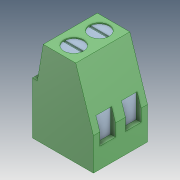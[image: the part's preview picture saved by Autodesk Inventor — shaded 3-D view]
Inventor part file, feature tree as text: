
AUTODESK INVENTOR PART (.ipt)
format: ipt  version: 2020 (Build 240168000, 168)  size: 202,752 bytes
history: native  units: in
note: dims shown in document units (in); Inventor stores cm internally (conversion verified against a paired STEP export)
features: extrude x6, sketch x5, plane x2, mirror x1
ambient origin geometry x8: Origin, YZ Plane, XZ Plane, XY Plane, X Axis, Y Axis, Z Axis, Center Point
bodies: Solid1 (feature_tree)
feature tree (14):
  extrude  "Extrusion1"  Depth=0.1299in
  plane  "Work Plane2"
  extrude  "Extrusion2"  Depth=0.0709in
  mirror  "Mirror1"
  extrude  "Extrusion3"  Depth=0.2441in
  sketch  "Sketch5"  dims[d6=0.0197in d7=0.2165in d8=0.0in]
  extrude  "Extrusion4"  Depth=0.2165in TaperAngle=0.0deg
  extrude  "Extrusion5"  Depth=0.0079in
  extrude  "Extrusion6"  Depth=0.0079in
  sketch  "Sketch1"  dims[d0=0.1299in d1=0.1299in]
  plane  "Work Plane1"
  sketch  "Sketch3"  dims[d2=0.3465in d3=0.0709in]
  sketch  "Sketch4"  dims[d4=0.2087in d5=0.2441in]
  sketch  "Sketch6"  dims[d9=0.05in d10=0.0079in d11=0.0079in d12=0.0394in d13=0.0394in d14=0.0906in d15=0.0in d16=0.063in d17=0.0984in d18=0.0394in d19=0.0197in d20=0.0in d21=0.0787in d22=0.0079in d23=0.0512in d24=0.0039in d25=0.0039in d26=0.0in d27=0.0079in d28=0.0in d29=0.0276in d30=0.1in d31=0.122in d32=0.0079in d33=0.0in]
